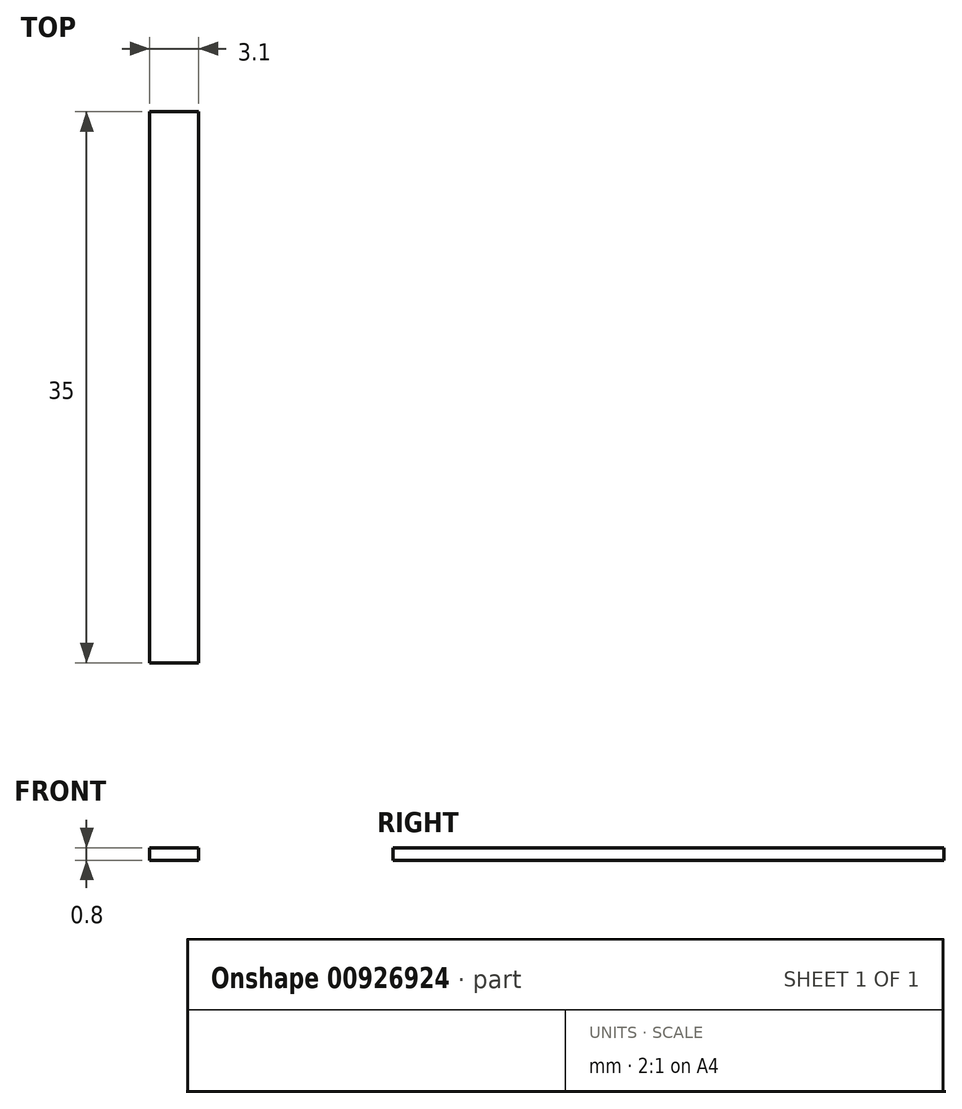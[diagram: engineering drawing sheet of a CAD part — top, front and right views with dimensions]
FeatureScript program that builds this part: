
annotation { "Feature Type Name" : "Feature", "Feature Type Description" : "" }
export const myFeature = defineFeature(function(context is Context, id is Id, definition is map)
    precondition{}
    {
        {
            var Q0;
            Q0=qCreatedBy(makeId("Top.planeOp"),FACE);
            var sketch = newSketch(context, id + "F0", { "sketchPlane" : qUnion([Q0])});
            skLineSegment(sketch, "E0.bottom", {"start": v(-1.55, 17.5) * mm, "end": v(1.55, 17.5) * mm});
            skLineSegment(sketch, "E0.top", {"start": v(-1.55, -17.5) * mm, "end": v(1.55, -17.5) * mm});
            skLineSegment(sketch, "E0.left", {"start": v(-1.55, 17.5) * mm, "end": v(-1.55, -17.5) * mm});
            skLineSegment(sketch, "E0.right", {"start": v(1.55, 17.5) * mm, "end": v(1.55, -17.5) * mm});
            skPoint(sketch, "E0.middle", {"position": v(0, 0) * mm});
            skSolve(sketch);
        }
        {
            var Q0;
            Q0=makeQuery(id+"F0.imprint","IMPRINT",FACE,{"disambiguationData":[TD([[makeQuery(id+"F0.imprint","IMPRINT",EDGE,{"derivedFrom":sQuery(id+"F0.wireOp",EDGE,"E0.bottom")}),-1.0]])]});
            extrude(context, id + "F1", {"entities" : qUnion([Q0]), "depth" : 0.8 * mm, "offsetDistance" : 25 * mm});
        }
    });
